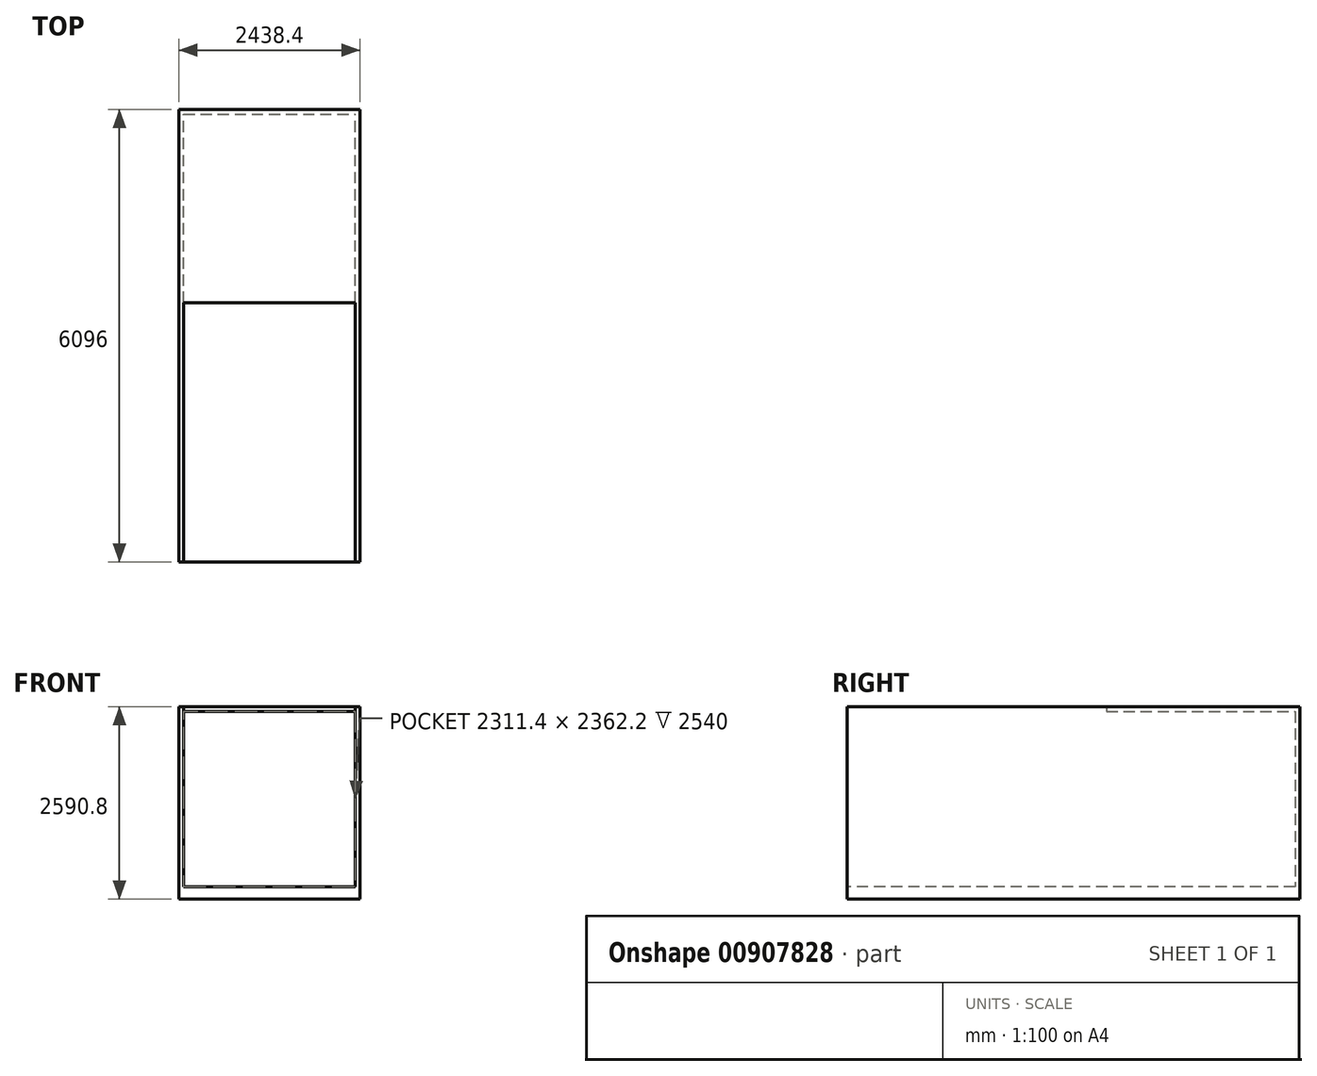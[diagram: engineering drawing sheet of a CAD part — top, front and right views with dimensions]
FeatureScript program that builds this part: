
annotation { "Feature Type Name" : "Feature", "Feature Type Description" : "" }
export const myFeature = defineFeature(function(context is Context, id is Id, definition is map)
    precondition{}
    {
        {
            var Q0;
            Q0=qCreatedBy(makeId("Front.planeOp"),FACE);
            var sketch = newSketch(context, id + "F0", { "sketchPlane" : qUnion([Q0])});
            skLineSegment(sketch, "E0.bottom", {"start": v(0, 0) * mm, "end": v(2438.4, 0) * mm});
            skLineSegment(sketch, "E0.top", {"start": v(0, 2590.8) * mm, "end": v(2438.4, 2590.8) * mm});
            skLineSegment(sketch, "E0.left", {"start": v(0, 0) * mm, "end": v(0, 2590.8) * mm});
            skLineSegment(sketch, "E0.right", {"start": v(2438.4, 0) * mm, "end": v(2438.4, 2590.8) * mm});
            skSolve(sketch);
        }
        {
            var Q0;
            Q0=makeQuery(id+"F0.imprint","IMPRINT",FACE,{"disambiguationData":[TD([[makeQuery(id+"F0.imprint","IMPRINT",EDGE,{"derivedFrom":sQuery(id+"F0.wireOp",EDGE,"E0.bottom")}),1.0]])]});
            var Q1;
            Q1 = qSketchRegion(id + "F2", true);
            extrude(context, id + "F1", {"entities" : qUnion([Q0, Q1]), "depth" : 6096 * mm, "offsetDistance" : 25.4 * mm});
        }
        {
            var Q0;
            Q0=makeQuery(id+"F1.opExtrude","CAP_FACE",FACE,{"disambiguationData":[OSD([sQuery(id+"F0.wireOp",EDGE,"E0.bottom"),sQuery(id+"F0.wireOp",EDGE,"E0.top"),sQuery(id+"F0.wireOp",EDGE,"E0.left"),sQuery(id+"F0.wireOp",EDGE,"E0.right")])],"isStart":false});
            var sketch = newSketch(context, id + "F2", { "sketchPlane" : qUnion([Q0])});
            skLineSegment(sketch, "E1.bottom", {"start": v(63.5, 2590.8) * mm, "end": v(2374.9, 2590.8) * mm});
            skLineSegment(sketch, "E1.top", {"start": v(63.5, 165.1) * mm, "end": v(2374.9, 165.1) * mm});
            skLineSegment(sketch, "E1.left", {"start": v(63.5, 2590.8) * mm, "end": v(63.5, 165.1) * mm});
            skLineSegment(sketch, "E1.right", {"start": v(2374.9, 2590.8) * mm, "end": v(2374.9, 165.1) * mm});
            skSolve(sketch);
        }
        {
            var Q0;
            Q0=makeQuery(id+"F2.imprint","IMPRINT",FACE,{"disambiguationData":[TD([[makeQuery(id+"F2.imprint","IMPRINT",EDGE,{"derivedFrom":sQuery(id+"F2.wireOp",EDGE,"E1.bottom")}),-1.0]])]});
            extrude(context, id + "F3", {"entities" : qUnion([Q0]), "operationType" : NewBodyOperationType.REMOVE, "oppositeDirection" : true, "depth" : 6032.5 * mm, "offsetDistance" : 25.4 * mm});
        }
        {
            var Q0;
            Q0=makeQuery(id+"F3.boolean.opBoolean","COPY",FACE,{"derivedFrom":makeQuery(id+"F3.opExtrude","CAP_FACE",FACE,{"disambiguationData":[OSD([sQuery(id+"F2.wireOp",EDGE,"E1.bottom"),sQuery(id+"F2.wireOp",EDGE,"E1.top"),sQuery(id+"F2.wireOp",EDGE,"E1.left"),sQuery(id+"F2.wireOp",EDGE,"E1.right")])],"isStart":false})});
            var sketch = newSketch(context, id + "F4", { "sketchPlane" : qUnion([Q0])});
            skLineSegment(sketch, "E2.bottom", {"start": v(63.5, 2590.8) * mm, "end": v(2374.9, 2590.8) * mm});
            skLineSegment(sketch, "E2.top", {"start": v(63.5, 2527.3) * mm, "end": v(2374.9, 2527.3) * mm});
            skLineSegment(sketch, "E2.left", {"start": v(63.5, 2590.8) * mm, "end": v(63.5, 2527.3) * mm});
            skLineSegment(sketch, "E2.right", {"start": v(2374.9, 2590.8) * mm, "end": v(2374.9, 2527.3) * mm});
            skSolve(sketch);
        }
        {
            var Q0;
            Q0=makeQuery(id+"F4.imprint","IMPRINT",FACE,{"disambiguationData":[TD([[makeQuery(id+"F4.imprint","IMPRINT",EDGE,{"derivedFrom":sQuery(id+"F4.wireOp",EDGE,"E2.bottom")}),-1.0]])]});
            extrude(context, id + "F5", {"entities" : qUnion([Q0]), "operationType" : NewBodyOperationType.ADD, "depth" : 2540 * mm, "offsetDistance" : 25.4 * mm});
        }
    });
